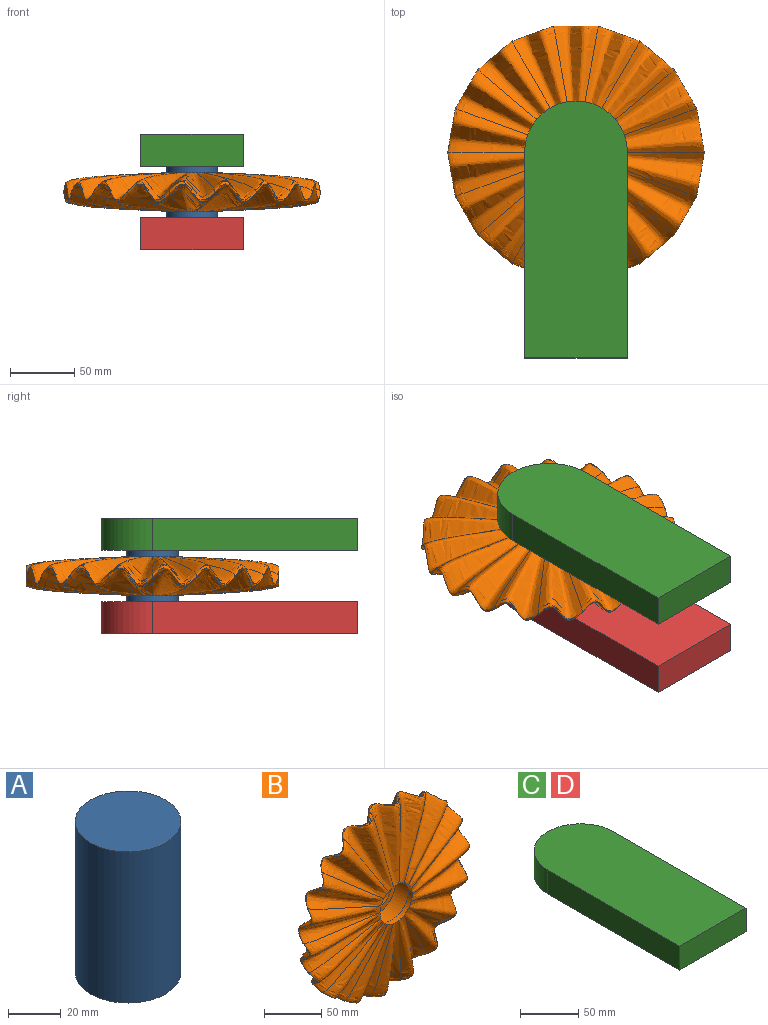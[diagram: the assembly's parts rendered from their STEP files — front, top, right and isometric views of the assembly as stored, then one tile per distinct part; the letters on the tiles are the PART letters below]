
ASSEMBLY  parts=4 mates=4
PART A: 3 faces, bbox 40x40x70 mm
  f0: cylinder r=20mm len=70mm, axis (0,0,-1), area 8796.5mm2, adj f1,f2
  f1: plane 40x40mm, normal (0,0,1), area 1256.6mm2, adj f0
  f2: plane 40x40mm, normal (0,0,-1), area 1256.6mm2, adj f0
PART B: 23 faces, bbox 280x30x275.7 mm
  f0: cylinder r=20mm len=40mm, axis (0,-1,0), area 628.3mm2, adj f2,f3,f4,f5,f6,f7,f8,f9
  f1: cylinder r=20mm len=40mm, axis (0,-1,0), area 628.3mm2, adj f2,f3,f4,f5,f6,f7,f8,f9
  f2: bspline ~118.18x48.62mm, area 4146.8mm2, adj f0,f1,f3,f19
  f3: bspline ~120.55x66.53mm, area 4146.8mm2, adj f0,f1,f2,f4
  f4: bspline ~108.39x97.25mm, area 4146.8mm2, adj f0,f1,f3,f5
  f5: bspline ~116.24x83.15mm, area 4146.8mm2, adj f0,f1,f4,f6
  f6: bspline ~121.21x47.88mm, area 4146.8mm2, adj f0,f1,f5,f7
  f7: bspline ~121.21x47.88mm, area 4146.8mm2, adj f0,f1,f6,f8
  f8: bspline ~116.24x83.15mm, area 4146.8mm2, adj f0,f1,f7,f9
  f9: bspline ~108.39x97.25mm, area 4146.8mm2, adj f0,f1,f8,f10
  f10: bspline ~120.55x66.53mm, area 4146.8mm2, adj f0,f1,f9,f11
  f11: bspline ~118.18x48.62mm, area 4146.8mm2, adj f0,f1,f10,f12
  f12: bspline ~120.55x66.53mm, area 4146.8mm2, adj f0,f1,f11,f13
  f13: bspline ~108.39x97.25mm, area 4146.8mm2, adj f0,f1,f12,f14
  f14: bspline ~116.24x83.15mm, area 4146.8mm2, adj f0,f1,f13,f15
  f15: bspline ~121.21x47.88mm, area 4146.8mm2, adj f0,f1,f14,f16
  f16: bspline ~121.21x47.88mm, area 4146.8mm2, adj f0,f1,f15,f17
  f17: bspline ~116.24x83.15mm, area 4146.8mm2, adj f0,f1,f16,f18
  f18: bspline ~108.39x97.25mm, area 4146.8mm2, adj f0,f1,f17,f19
  f19: bspline ~120.55x66.53mm, area 4146.8mm2, adj f0,f1,f2,f18
  f20: plane 50x50mm, normal (0,-1,0), area 706.9mm2, adj f1,f21
  f21: cylinder r=25mm len=50mm, axis (0,-1,0), area 3141.6mm2, adj f20,f22
  f22: plane 50x50mm, normal (0,1,0), area 706.9mm2, adj f0,f21
PART C: 8 faces, bbox 80x200x25 mm
  f0: cylinder r=40mm len=80mm, axis (0,0,-1), area 3141.6mm2, adj f1,f3,f4,f5
  f1: plane 160x25mm, normal (-1,0,0), area 4000mm2, adj f0,f2,f4,f5
  f2: plane 80x25mm, normal (0,-1,0), area 2000mm2, adj f1,f3,f4,f5
  f3: plane 160x25mm, normal (1,0,0), area 4000mm2, adj f0,f2,f4,f5
  f4: plane 200x80mm, normal (0,0,1), area 15313.3mm2, adj f0,f1,f2,f3
  f5: plane 200x80mm, normal (0,0,-1), area 14056.6mm2, adj f0,f1,f2,f3,f6
  f6: cylinder r=20mm len=40mm, axis (0,0,-1), area 1885mm2, adj f5,f7
  f7: plane 40x40mm, normal (0,0,-1), area 1256.6mm2, adj f6
PART D: same geometry as C
PLACE A t=(86.7,411.23,-98.51)mm
PLACE B rot(axis=(1,0,0),90deg) t=(48.54,286.7,-63.51)mm
PLACE C t=(96.7,359.13,-43.51)mm
PLACE D rot(axis=(0,-1,0),180deg) t=(0.38,359.13,-83.51)mm
MATE planar A.f0 <-> C.f0  axis (0,0,1) through (48.54,385.18,-28.51)mm
MATE planar A.f0 <-> D.f0  axis (0,0,-1) through (48.54,385.18,-98.51)mm
MATE parallel C.f5 <-> D.f5  axis (0,0,-1) through (48.54,315.37,-43.51)mm
MATE revolute A.f0 <-> B.f0  axis (0,0,-1) through (48.54,385.18,-63.51)mm
